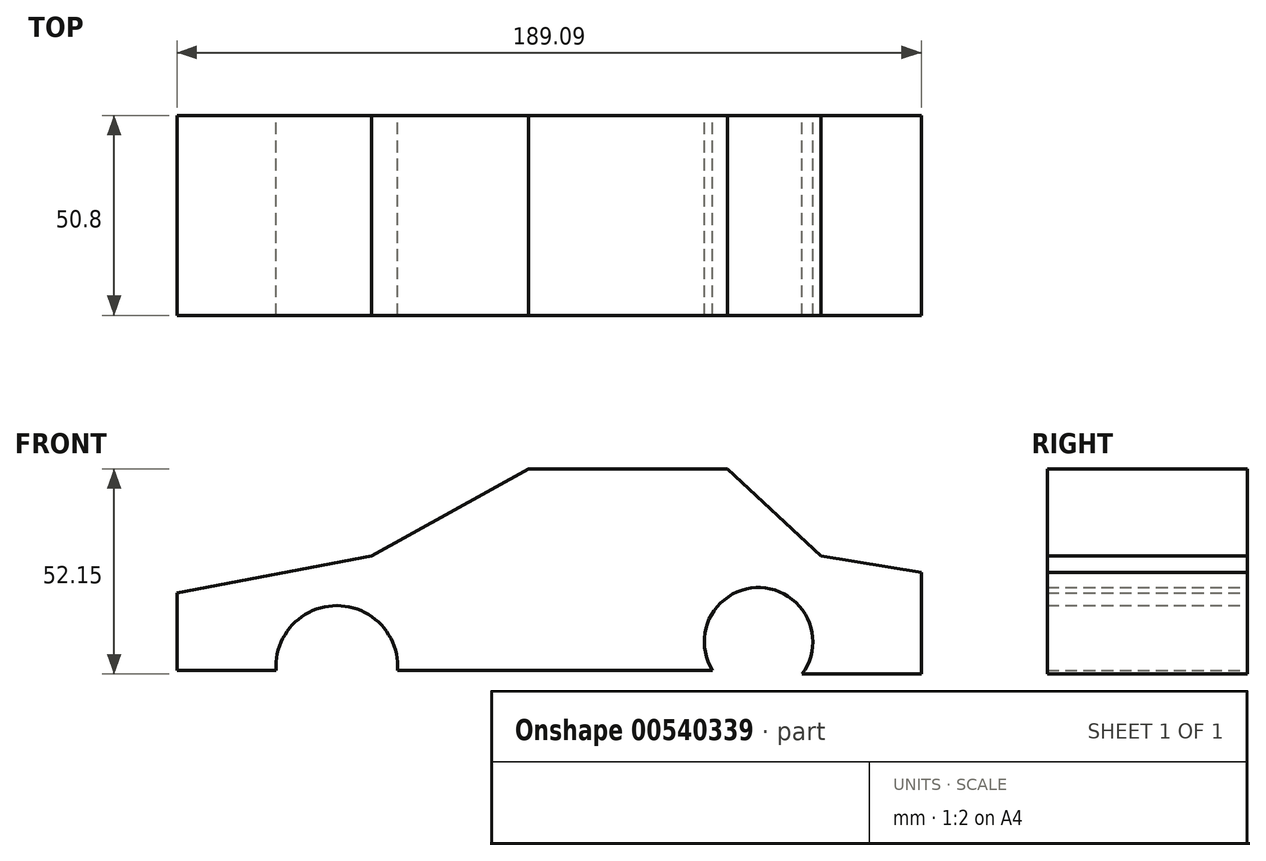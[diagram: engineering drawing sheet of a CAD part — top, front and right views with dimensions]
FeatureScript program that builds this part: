
annotation { "Feature Type Name" : "Feature", "Feature Type Description" : "" }
export const myFeature = defineFeature(function(context is Context, id is Id, definition is map)
    precondition{}
    {
        {
            var Q0;
            Q0=qCreatedBy(makeId("Front.planeOp"),FACE);
            var sketch = newSketch(context, id + "F0", { "sketchPlane" : qUnion([Q0])});
            skLineSegment(sketch, "E0", {"start": v(-48.25, 0) * mm, "end": v(-8.4, 22.18) * mm});
            skLineSegment(sketch, "E1", {"start": v(-8.4, 22.18) * mm, "end": v(42.1, 22.18) * mm});
            skLineSegment(sketch, "E2", {"start": v(42.1, 22.18) * mm, "end": v(65.93, 0) * mm});
            skLineSegment(sketch, "E3", {"start": v(65.93, 0) * mm, "end": v(91.4, -4.2) * mm});
            skLineSegment(sketch, "E4", {"start": v(91.4, -4.2) * mm, "end": v(91.4, -29.97) * mm});
            skLineSegment(sketch, "E5", {"start": v(91.4, -29.97) * mm, "end": v(61.13, -29.97) * mm});
            skLineSegment(sketch, "E6", {"start": v(-48.25, 0) * mm, "end": v(-97.7, -9.29) * mm});
            skLineSegment(sketch, "E7", {"start": v(-97.7, -9.29) * mm, "end": v(-97.7, -29.07) * mm});
            skLineSegment(sketch, "E8", {"start": v(-97.7, -29.07) * mm, "end": v(-72.52, -29.07) * mm});
            skLineSegment(sketch, "E9", {"start": v(-41.65, -29.07) * mm, "end": v(38.36, -29.07) * mm});
            skArc(sketch, "E10", {"start": v(-41.65, -29.07) * mm, "mid": v(-57.09, -12.59) * mm, "end": v(-72.52, -29.07) * mm});
            skArc(sketch, "E11", {"start": v(61.13, -29.97) * mm, "mid": v(50.6, -8) * mm, "end": v(38.36, -29.07) * mm});
            skSolve(sketch);
        }
        {
            var Q0;
            Q0=makeQuery(id+"F0.imprint","IMPRINT",FACE,{"disambiguationData":[TD([[makeQuery(id+"F0.imprint","IMPRINT",EDGE,{"derivedFrom":sQuery(id+"F0.wireOp",EDGE,"E0")}),-1.0]])]});
            extrude(context, id + "F1", {"entities" : qUnion([Q0]), "depth" : 25.4 * mm, "offsetDistance" : 25.4 * mm, "hasSecondDirection" : true, "secondDirectionOppositeDirection" : true, "secondDirectionDepth" : 25.4 * mm});
        }
    });
